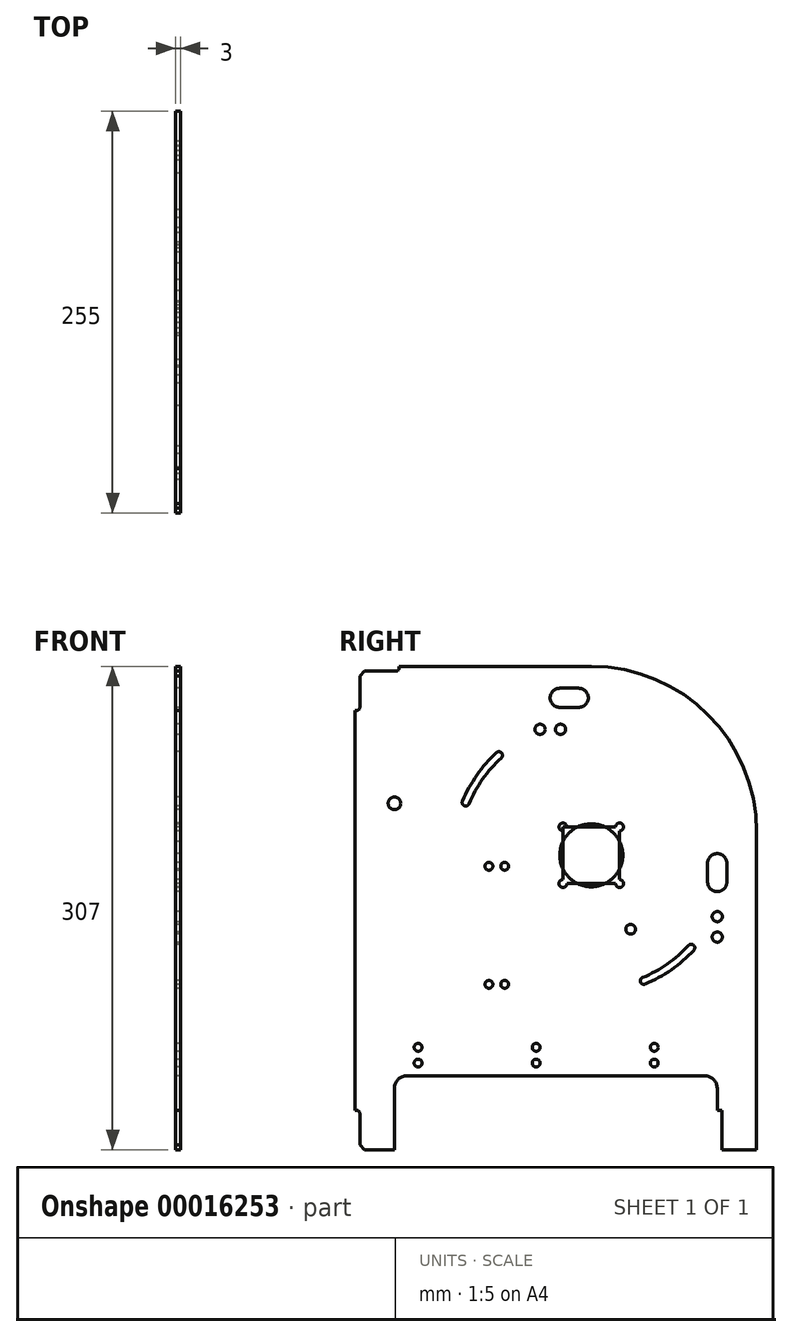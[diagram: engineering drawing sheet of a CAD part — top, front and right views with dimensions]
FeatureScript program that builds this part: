
annotation { "Feature Type Name" : "Feature", "Feature Type Description" : "" }
export const myFeature = defineFeature(function(context is Context, id is Id, definition is map)
    precondition{}
    {
        {
            assignVariable(context, id + "F0", {"variableType" : VariableType.LENGTH, "name" : "Thickness", "lengthValue" : 3 * mm});
        }
        {
            var Q0;
            Q0=qCreatedBy(makeId("Right.planeOp"),FACE);
            var sketch = newSketch(context, id + "F1", { "sketchPlane" : qUnion([Q0])});
            skLineSegment(sketch, "E0", {"start": v(0, 282) * mm, "end": v(0, 28) * mm});
            skLineSegment(sketch, "E1", {"start": v(0, 28) * mm, "end": v(1, 28) * mm});
            skArc(sketch, "E2", {"start": v(1, 28) * mm, "mid": v(2.41, 27.41) * mm, "end": v(3, 26) * mm});
            skLineSegment(sketch, "E3", {"start": v(3, 26) * mm, "end": v(3, 6) * mm});
            skLineSegment(sketch, "E4", {"start": v(-124.5, -150.5) * mm, "end": v(-121.5, -153.5) * mm});
            skLineSegment(sketch, "E5", {"start": v(6, 3) * mm, "end": v(25, 3) * mm});
            skLineSegment(sketch, "E6", {"start": v(25, 3) * mm, "end": v(25, 42) * mm});
            skLineSegment(sketch, "E7", {"start": v(33, 50) * mm, "end": v(222, 50) * mm});
            skLineSegment(sketch, "E8", {"start": v(230, 42) * mm, "end": v(230, 28) * mm});
            skLineSegment(sketch, "E9", {"start": v(230, 28) * mm, "end": v(233, 28) * mm});
            skArc(sketch, "E10", {"start": v(103.5, -128.5) * mm, "mid": v(104.91, -129.09) * mm, "end": v(105.5, -130.5) * mm});
            skLineSegment(sketch, "E11", {"start": v(233, 28) * mm, "end": v(233, 3) * mm});
            skLineSegment(sketch, "E12", {"start": v(105.5, -150.5) * mm, "end": v(108.5, -153.5) * mm});
            skLineSegment(sketch, "E13", {"start": v(233, 3) * mm, "end": v(255, 3) * mm});
            skLineSegment(sketch, "E14", {"start": v(255, 3) * mm, "end": v(255, 205) * mm});
            skArc(sketch, "E15", {"start": v(255, 205) * mm, "mid": v(224.25, 279.25) * mm, "end": v(150, 310) * mm});
            skLineSegment(sketch, "E16", {"start": v(150, 310) * mm, "end": v(28, 310) * mm});
            skLineSegment(sketch, "E17", {"start": v(28, 310) * mm, "end": v(28, 309) * mm});
            skArc(sketch, "E18", {"start": v(28, 309) * mm, "mid": v(27.41, 307.59) * mm, "end": v(26, 307) * mm});
            skLineSegment(sketch, "E19", {"start": v(26, 307) * mm, "end": v(6, 307) * mm});
            skLineSegment(sketch, "E20", {"start": v(3, 304) * mm, "end": v(3, 284) * mm});
            skArc(sketch, "E21", {"start": v(3, 284) * mm, "mid": v(2.41, 282.59) * mm, "end": v(1, 282) * mm});
            skLineSegment(sketch, "E22", {"start": v(1, 282) * mm, "end": v(0, 282) * mm});
            skArc(sketch, "E23", {"start": v(130, 296.1) * mm, "mid": v(123.9, 290) * mm, "end": v(130, 283.9) * mm});
            skLineSegment(sketch, "E24", {"start": v(130, 283.9) * mm, "end": v(142, 283.9) * mm});
            skArc(sketch, "E25", {"start": v(142, 283.9) * mm, "mid": v(148.1, 290) * mm, "end": v(142, 296.1) * mm});
            skLineSegment(sketch, "E26", {"start": v(142, 296.1) * mm, "end": v(130, 296.1) * mm});
            skCircle(sketch, "E27", {"center": v(130.5, 270) * mm, "radius": 3.25 * mm});
            skCircle(sketch, "E28", {"center": v(117.5, 270) * mm, "radius": 3.25 * mm});
            skArc(sketch, "E29", {"start": v(89.8, 255.21) * mm, "mid": v(77.33, 240.95) * mm, "end": v(68.18, 224.38) * mm});
            skArc(sketch, "E30", {"start": v(68.18, 224.38) * mm, "mid": v(69.38, 221.43) * mm, "end": v(72.33, 222.63) * mm});
            skArc(sketch, "E31", {"start": v(72.33, 222.63) * mm, "mid": v(81.02, 238.37) * mm, "end": v(92.85, 251.9) * mm});
            skArc(sketch, "E32", {"start": v(92.85, 251.9) * mm, "mid": v(92.98, 255.08) * mm, "end": v(89.8, 255.21) * mm});
            skCircle(sketch, "E33", {"center": v(25, 223) * mm, "radius": 4 * mm});
            skCircle(sketch, "E34", {"center": v(85, 183) * mm, "radius": 2.5 * mm});
            skCircle(sketch, "E35", {"center": v(95, 183) * mm, "radius": 2.5 * mm});
            skCircle(sketch, "E36", {"center": v(132, 208) * mm, "radius": 2.5 * mm});
            skCircle(sketch, "E37", {"center": v(150, 190) * mm, "radius": 20 * mm});
            skCircle(sketch, "E38", {"center": v(132, 172) * mm, "radius": 2.5 * mm});
            skCircle(sketch, "E39", {"center": v(168, 172) * mm, "radius": 2.5 * mm});
            skCircle(sketch, "E40", {"center": v(168, 208) * mm, "radius": 2.5 * mm});
            skCircle(sketch, "E41", {"center": v(95, 108) * mm, "radius": 2.5 * mm});
            skCircle(sketch, "E42", {"center": v(85, 108) * mm, "radius": 2.5 * mm});
            skCircle(sketch, "E43", {"center": v(40, 68) * mm, "radius": 2.5 * mm});
            skCircle(sketch, "E44", {"center": v(40, 58) * mm, "radius": 2.5 * mm});
            skCircle(sketch, "E45", {"center": v(115, 68) * mm, "radius": 2.5 * mm});
            skCircle(sketch, "E46", {"center": v(115, 58) * mm, "radius": 2.5 * mm});
            skCircle(sketch, "E47", {"center": v(190, 68) * mm, "radius": 2.5 * mm});
            skCircle(sketch, "E48", {"center": v(190, 58) * mm, "radius": 2.5 * mm});
            skArc(sketch, "E49", {"start": v(211.83, 132.77) * mm, "mid": v(198.28, 120.95) * mm, "end": v(182.53, 112.28) * mm});
            skArc(sketch, "E50", {"start": v(182.53, 112.28) * mm, "mid": v(181.32, 109.34) * mm, "end": v(184.26, 108.13) * mm});
            skArc(sketch, "E51", {"start": v(184.26, 108.13) * mm, "mid": v(200.86, 117.27) * mm, "end": v(215.13, 129.71) * mm});
            skArc(sketch, "E52", {"start": v(215.13, 129.71) * mm, "mid": v(215, 132.9) * mm, "end": v(211.83, 132.77) * mm});
            skCircle(sketch, "E53", {"center": v(230, 138) * mm, "radius": 3.25 * mm});
            skCircle(sketch, "E54", {"center": v(230, 151) * mm, "radius": 3.25 * mm});
            skArc(sketch, "E55", {"start": v(236.1, 173) * mm, "mid": v(230, 166.9) * mm, "end": v(223.9, 173) * mm});
            skLineSegment(sketch, "E56", {"start": v(223.9, 173) * mm, "end": v(223.9, 185) * mm});
            skArc(sketch, "E57", {"start": v(223.9, 185) * mm, "mid": v(230, 191.1) * mm, "end": v(236.1, 185) * mm});
            skLineSegment(sketch, "E58", {"start": v(236.1, 185) * mm, "end": v(236.1, 173) * mm});
            skCircle(sketch, "E59", {"center": v(175, 143) * mm, "radius": 3.1 * mm});
            skLineSegment(sketch, "E60", {"start": v(40, 68) * mm, "end": v(190, 68) * mm, "construction": true});
            skLineSegment(sketch, "E61", {"start": v(40, 58) * mm, "end": v(190, 58) * mm, "construction": true});
            skLineSegment(sketch, "E62", {"start": v(85, 183) * mm, "end": v(85, 108) * mm, "construction": true});
            skLineSegment(sketch, "E63", {"start": v(95, 108) * mm, "end": v(95, 183) * mm, "construction": true});
            skLineSegment(sketch, "E64.bottom", {"start": v(132, 208) * mm, "end": v(168, 208) * mm});
            skLineSegment(sketch, "E64.top", {"start": v(132, 172) * mm, "end": v(168, 172) * mm});
            skLineSegment(sketch, "E64.left", {"start": v(132, 208) * mm, "end": v(132, 172) * mm});
            skLineSegment(sketch, "E64.right", {"start": v(168, 208) * mm, "end": v(168, 172) * mm});
            skLineSegment(sketch, "E65", {"start": v(150, 190) * mm, "end": v(183.4, 110.2) * mm, "construction": true});
            skLineSegment(sketch, "E66", {"start": v(213.48, 131.24) * mm, "end": v(150, 190) * mm, "construction": true});
            skLineSegment(sketch, "E67", {"start": v(150, 190) * mm, "end": v(91.33, 253.56) * mm, "construction": true});
            skLineSegment(sketch, "E68", {"start": v(150, 190) * mm, "end": v(70.25, 223.5) * mm, "construction": true});
            skLineSegment(sketch, "E69", {"start": v(230, 138) * mm, "end": v(230, 151) * mm, "construction": true});
            skLineSegment(sketch, "E70", {"start": v(230, 173) * mm, "end": v(230, 185) * mm, "construction": true});
            skLineSegment(sketch, "E71", {"start": v(117.5, 270) * mm, "end": v(130.5, 270) * mm, "construction": true});
            skLineSegment(sketch, "E72", {"start": v(130, 290) * mm, "end": v(142, 290) * mm, "construction": true});
            skLineSegment(sketch, "E73", {"start": v(-30.33, 0) * mm, "end": v(276.91, 0) * mm, "construction": true});
            skLineSegment(sketch, "E74", {"start": v(-47.16, 190) * mm, "end": v(358.12, 190) * mm, "construction": true});
            skLineSegment(sketch, "E75", {"start": v(150, 371.4) * mm, "end": v(150, -29.36) * mm, "construction": true});
            skLineSegment(sketch, "E76", {"start": v(95, 108) * mm, "end": v(85, 108) * mm, "construction": true});
            skLineSegment(sketch, "E77", {"start": v(40, 58) * mm, "end": v(40, 68) * mm, "construction": true});
            skPoint(sketch, "E78", {"position": v(28, 309) * mm});
            skLineSegment(sketch, "E79", {"start": v(3, 6) * mm, "end": v(6, 3) * mm});
            skPoint(sketch, "E80.visualSharp", {"position": v(230, 50) * mm});
            skArc(sketch, "E80.filletArc", {"start": v(230, 42) * mm, "mid": v(227.66, 47.66) * mm, "end": v(222, 50) * mm});
            skPoint(sketch, "E81.visualSharp", {"position": v(25, 50) * mm});
            skArc(sketch, "E81.filletArc", {"start": v(33, 50) * mm, "mid": v(27.34, 47.66) * mm, "end": v(25, 42) * mm});
            skLineSegment(sketch, "E82", {"start": v(3, 304) * mm, "end": v(6, 307) * mm});
            skCircle(sketch, "E83", {"center": v(150, 190) * mm, "radius": 86.5 * mm, "construction": true});
            skSolve(sketch);
        }
        {
            var Q0;
            Q0=makeQuery(id+"F1.imprint","IMPRINT",FACE,{"disambiguationData":[TD([[makeQuery(id+"F1.imprint","IMPRINT",EDGE,{"derivedFrom":sQuery(id+"F1.wireOp",EDGE,"E0")}),1.0]])]});
            var Q1;
            {var subQ0=sQuery(id+"F1.wireOp",EDGE,"E64.bottom");var subQ1=sQuery(id+"F1.wireOp",EDGE,"E37");var subQ2=makeQuery(id+"F1.imprint","INTERSECT",VERTEX,{"disambiguationData":[OD(1.0)],"derivedFrom":[subQ1,subQ0]});Q1=makeQuery(id+"F1.imprint","IMPRINT",FACE,{"disambiguationData":[TD([[makeQuery(id+"F1.imprint","IMPRINT",EDGE,{"disambiguationData":[TD([[subQ2,-1.0]])],"derivedFrom":subQ1}),1.0]])]});}
            var Q2;
            {var subQ0=sQuery(id+"F1.wireOp",EDGE,"E64.top");var subQ1=sQuery(id+"F1.wireOp",EDGE,"E37");var subQ2=makeQuery(id+"F1.imprint","INTERSECT",VERTEX,{"disambiguationData":[OD(0.0)],"derivedFrom":[subQ1,subQ0]});Q2=makeQuery(id+"F1.imprint","IMPRINT",FACE,{"disambiguationData":[TD([[makeQuery(id+"F1.imprint","IMPRINT",EDGE,{"disambiguationData":[TD([[subQ2,1.0]])],"derivedFrom":subQ1}),1.0]])]});}
            var Q3;
            {var subQ0=sQuery(id+"F1.wireOp",EDGE,"E64.top");var subQ1=sQuery(id+"F1.wireOp",EDGE,"E37");var subQ2=makeQuery(id+"F1.imprint","INTERSECT",VERTEX,{"disambiguationData":[OD(1.0)],"derivedFrom":[subQ1,subQ0]});Q3=makeQuery(id+"F1.imprint","IMPRINT",FACE,{"disambiguationData":[TD([[makeQuery(id+"F1.imprint","IMPRINT",EDGE,{"disambiguationData":[TD([[subQ2,-1.0]])],"derivedFrom":subQ1}),1.0]])]});}
            var Q4;
            {var subQ0=sQuery(id+"F1.wireOp",EDGE,"E64.bottom");var subQ1=sQuery(id+"F1.wireOp",EDGE,"E36");var subQ2=makeQuery(id+"F1.imprint","INTERSECT",VERTEX,{"derivedFrom":[subQ1,subQ0]});Q4=makeQuery(id+"F1.imprint","IMPRINT",FACE,{"disambiguationData":[TD([[makeQuery(id+"F1.imprint","IMPRINT",EDGE,{"disambiguationData":[TD([[subQ2,-1.0]])],"derivedFrom":subQ1}),1.0]])]});}
            extrude(context, id + "F2", {"entities" : qUnion([Q0, Q1, Q2, Q3, Q4]), "depth" : getVariable(context, 'Thickness'), "offsetDistance" : 25 * mm});
        }
    });
